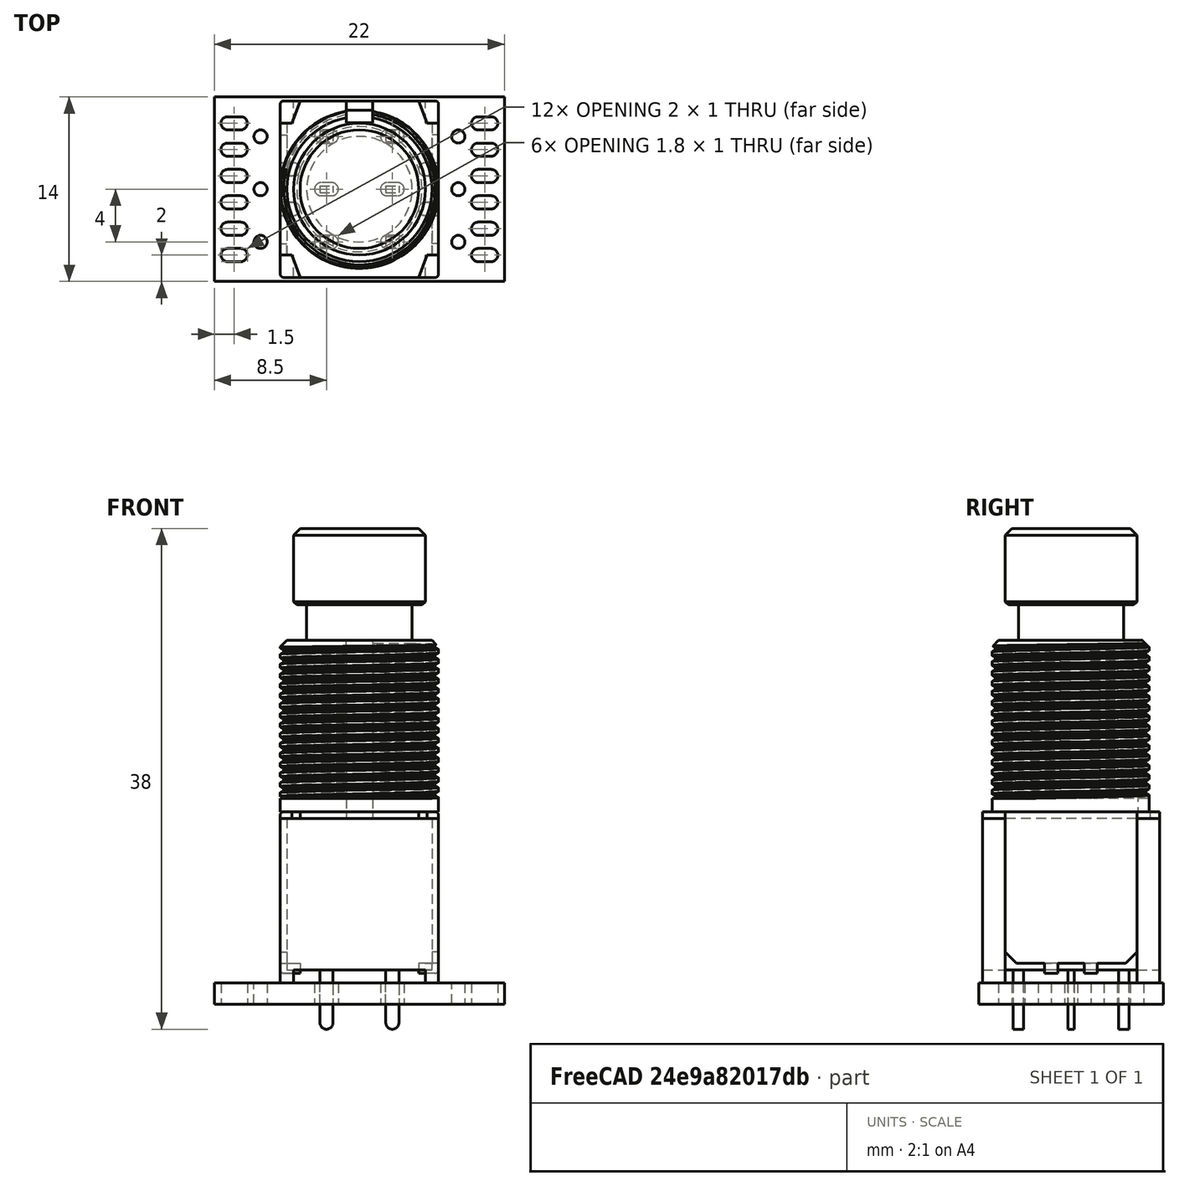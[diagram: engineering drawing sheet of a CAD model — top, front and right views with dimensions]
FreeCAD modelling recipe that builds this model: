
FCSTD DOCUMENT  (FreeCAD 0.18R16131 (Git))
Label: #400-000 - Switching PCBA [Alpha DPDT]
License: All rights reserved
LicenseURL: http://en.wikipedia.org/wiki/All_rights_reserved
objects: App::Part×4, Part::Feature×2, PartDesign::CoordinateSystem×1, Sketcher::SketchObject×1
note: 4 computed .brp shape members not serialized (recipe doc carries the construction recipe); baked Part::Feature solids carry a one-line shape summary decoded from their .brp

FEATURE [PartDesign::CoordinateSystem] Local_CS
  AttacherType = Attacher::AttachEngine3D
FEATURE [Part::Feature] Pcb
  Placement = pos=(-146.05,90.17,0) rot=(0,0,1;0rad)
  shape: bbox 22 x 14 x 1.6 mm, 120 faces (baked)
FEATURE [Sketcher::SketchObject] PCB_Sketch
  sketch-geometry (4):
    g0: LineSegment StartX=-11 StartY=-7 StartZ=0 EndX=-11 EndY=7 EndZ=0
    g1: LineSegment StartX=11 StartY=-7 StartZ=0 EndX=-11 EndY=-7 EndZ=0
    g2: LineSegment StartX=11 StartY=7 StartZ=0 EndX=11 EndY=-7 EndZ=0
    g3: LineSegment StartX=-11 StartY=7 StartZ=0 EndX=11 EndY=7 EndZ=0
  constraints (4):
    c: Coincident(g0,g1)
    c: Coincident(g0,g3)
    c: Coincident(g1,g2)
    c: Coincident(g2,g3)
FEATURE [App::Part] Board_Geoms
  Group = -> [Local_CS,Pcb,PCB_Sketch]
  Origin = -> Origin
FEATURE [Part::Feature] Shape  label="SW1_Alpha Taiwan SF12011-0202-20R-X_5DFC3402"
  shape: bbox 15.12 x 14.87 x 38 mm, 238 faces, 10 solids (baked)
FEATURE [App::Part] Top
  Group = -> [Shape]
  Origin = -> Origin003
FEATURE [App::Part] Step_Models
  Group = -> [Top]
  Origin = -> Origin002
FEATURE [App::Part] Board  label="#400-000 - Switching PCBA [Alpha DPDT]"
  Group = -> [Board_Geoms,Step_Models]
  Origin = -> Origin001
